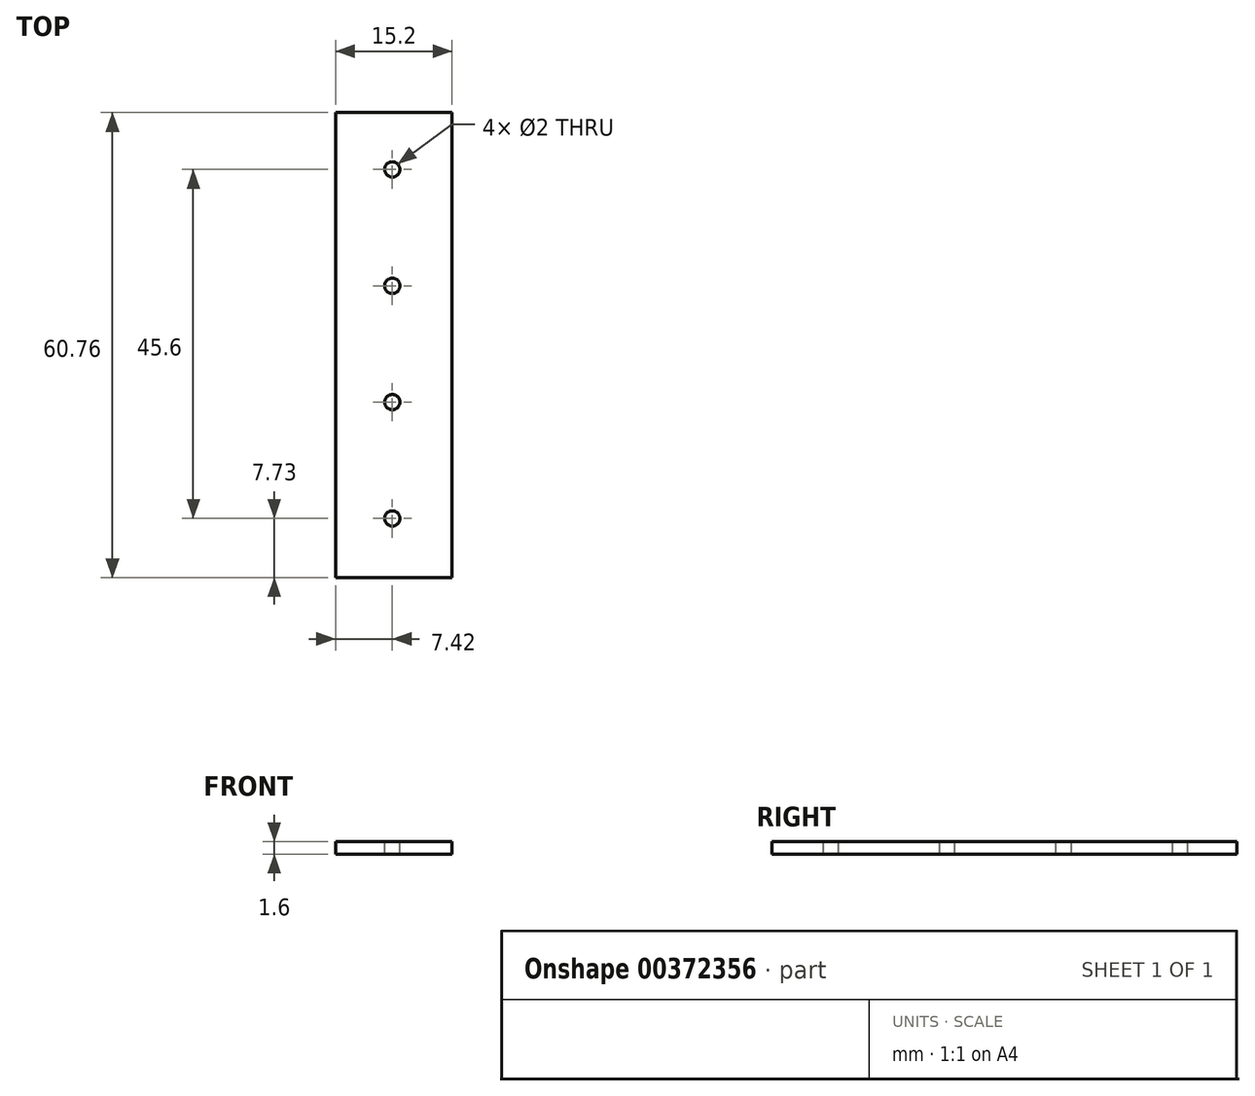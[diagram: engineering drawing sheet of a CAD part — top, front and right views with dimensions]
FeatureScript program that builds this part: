
annotation { "Feature Type Name" : "Feature", "Feature Type Description" : "" }
export const myFeature = defineFeature(function(context is Context, id is Id, definition is map)
    precondition{}
    {
        {
            var Q0;
            Q0=qCreatedBy(makeId("Top.planeOp"),FACE);
            var sketch = newSketch(context, id + "F0", { "sketchPlane" : qUnion([Q0])});
            skCircle(sketch, "E0", {"center": v(0, 0) * mm, "radius": 1 * mm});
            skCircle(sketch, "E1.0.1.0", {"center": v(0, 15.2) * mm, "radius": 1 * mm});
            skCircle(sketch, "E1.0.2.0", {"center": v(0, 30.4) * mm, "radius": 1 * mm});
            skLineSegment(sketch, "E1.direction1", {"start": v(0, 0) * mm, "end": v(25, 0) * mm, "construction": true});
            skLineSegment(sketch, "E1.direction2", {"start": v(0, 0) * mm, "end": v(0, 15.2) * mm, "construction": true});
            skCircle(sketch, "E2.0.1.0", {"center": v(0, -15.2) * mm, "radius": 1 * mm});
            skLineSegment(sketch, "E2.direction2", {"start": v(0, 0) * mm, "end": v(0, -15.2) * mm, "construction": true});
            skSolve(sketch);
        }
        {
            var Q0;
            Q0=qCreatedBy(makeId("Top.planeOp"),FACE);
            var sketch = newSketch(context, id + "F1", { "sketchPlane" : qUnion([Q0])});
            skLineSegment(sketch, "E3.bottom", {"start": v(-7.42, 37.83) * mm, "end": v(7.78, 37.83) * mm});
            skLineSegment(sketch, "E3.top", {"start": v(-7.42, -22.93) * mm, "end": v(7.78, -22.93) * mm});
            skLineSegment(sketch, "E3.left", {"start": v(-7.42, 37.83) * mm, "end": v(-7.42, -22.93) * mm});
            skLineSegment(sketch, "E3.right", {"start": v(7.78, 37.83) * mm, "end": v(7.78, -22.93) * mm});
            skSolve(sketch);
        }
        {
            var Q0;
            Q0 = qSketchRegion(id + "F1", true);
            extrude(context, id + "F2", {"entities" : qUnion([Q0]), "oppositeDirection" : true, "depth" : 1.6 * mm});
        }
        {
            var Q0;
            Q0 = qSketchRegion(id + "F0", true);
            extrude(context, id + "F3", {"entities" : qUnion([Q0]), "operationType" : NewBodyOperationType.REMOVE, "oppositeDirection" : true, "depth" : 25 * mm});
        }
    });
